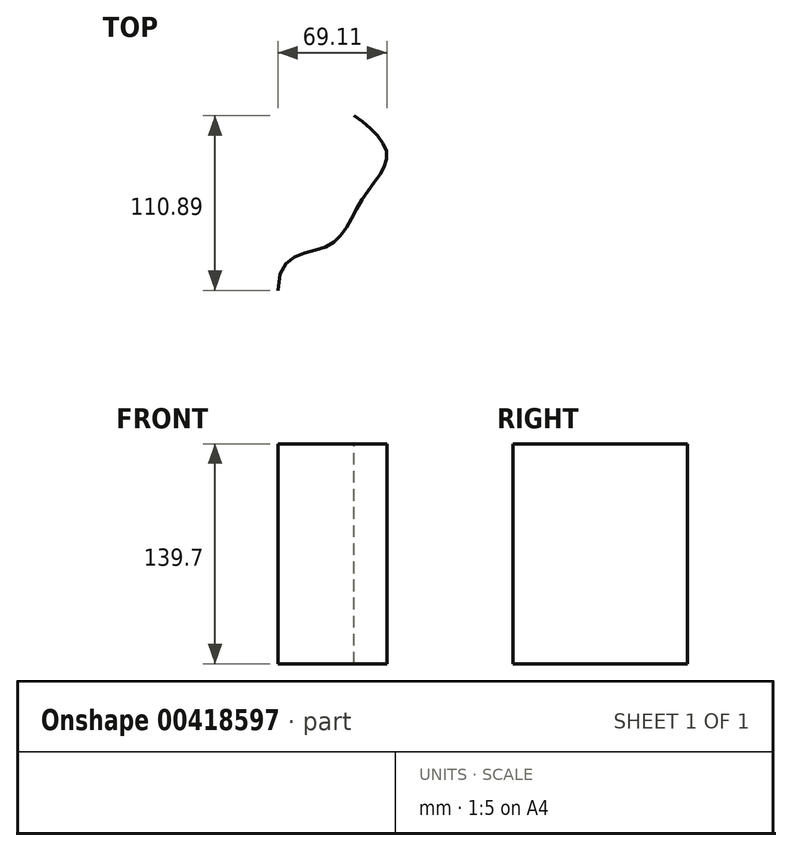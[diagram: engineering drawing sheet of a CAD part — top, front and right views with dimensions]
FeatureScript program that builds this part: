
annotation { "Feature Type Name" : "Feature", "Feature Type Description" : "" }
export const myFeature = defineFeature(function(context is Context, id is Id, definition is map)
    precondition{}
    {
        {
            var Q0;
            Q0=qCreatedBy(makeId("Top.planeOp"),FACE);
            var sketch = newSketch(context, id + "F0", { "sketchPlane" : qUnion([Q0])});
            skFitSpline(sketch, "E0", {"points": [v(-80.4, -58.13) * mm, v(-48.94, -30.06) * mm, v(-26.84, 0) * mm, v(-11.3, 27.8) * mm, v(-32.2, 52.76) * mm], "startDerivative": vector(-4.92, 286.45) * mm, "endDerivative": vector(-123.8, 80) * mm});
            skLineSegment(sketch, "E1", {"start": v(-197.72, 50.8) * mm, "end": v(182.55, 50.8) * mm, "construction": true});
            skLineSegment(sketch, "E2", {"start": v(-196.56, -50.8) * mm, "end": v(186.62, -50.8) * mm, "construction": true});
            skSolve(sketch);
        }
        {
            var Q0;
            Q0=sQuery(id+"F0.wireOp",EDGE,"E0");
            extrude(context, id + "F1", {"bodyType" : ToolBodyType.SURFACE, "surfaceEntities" : qUnion([Q0]), "depth" : 139.7 * mm});
        }
    });
